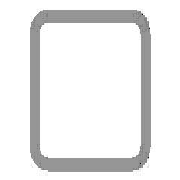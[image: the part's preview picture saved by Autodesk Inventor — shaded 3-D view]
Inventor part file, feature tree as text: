
AUTODESK INVENTOR PART (.ipt)
format: ipt  version: 2022.1 (Build 261234000, 234)  size: 135,680 bytes
history: native  units: mm (DEFAULTED — no unit token found)
features: other x4, sketch x3, extrude x1, plane x1
ambient origin geometry x8: Origin, YZ Plane, XZ Plane, XY Plane, X Axis, Y Axis, Z Axis, Center Point
bodies: Solid1 (feature_tree)
feature tree (9):
  parser-record x1  (decoder bookkeeping rows leaked as tree rows — omitted from the tree; the rows remain in map.json)
  other  "Driven Length"
  other  "Plano inicial"
  other  "Plano final"
  extrude  "Cuerpo"  TaperAngle=0.0deg  [1 undecoded]
  sketch  "Boceto"  dims[d10=40.0mm d11=40.0mm d12=5.0mm d13=-0.0mm d14=180.277564mm d15=20.0mm d16=20.0mm d17=90.0deg d18=180.277564mm]
  sketch  "Sketch3"  dims[d3=180.277564mm d4=0.0mm]
  plane  "Work Plane3"
  sketch  "Sketch4"  dims[d7=7.5mm]
note: 1 required parameter value undecoded (feature->parameter linkage not recoverable at this tier; creation-order binding heuristic only, values carry confidence <= 0.55)
